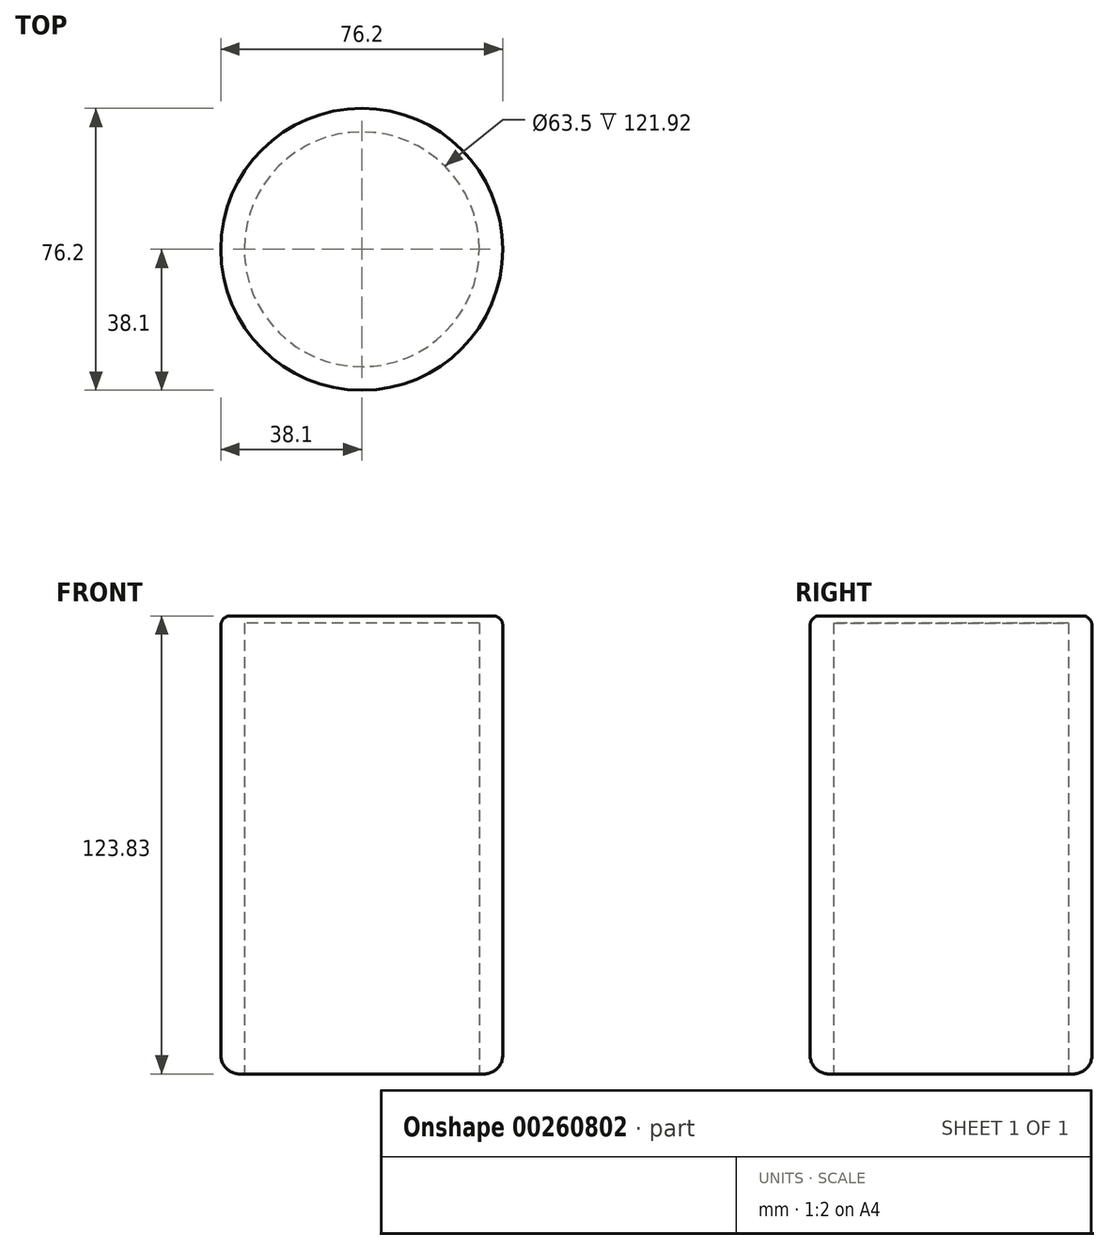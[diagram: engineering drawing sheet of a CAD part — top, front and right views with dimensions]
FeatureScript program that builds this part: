
annotation { "Feature Type Name" : "Feature", "Feature Type Description" : "" }
export const myFeature = defineFeature(function(context is Context, id is Id, definition is map)
    precondition{}
    {
        {
            var Q0;
            Q0=qCreatedBy(makeId("Top.planeOp"),FACE);
            var sketch = newSketch(context, id + "F0", { "sketchPlane" : qUnion([Q0])});
            skCircle(sketch, "E0", {"center": v(0, 0) * mm, "radius": 38.1 * mm});
            skSolve(sketch);
        }
        {
            var Q0;
            Q0=qCreatedBy(makeId("Top.planeOp"),FACE);
            var sketch = newSketch(context, id + "F1", { "sketchPlane" : qUnion([Q0])});
            skCircle(sketch, "E1", {"center": v(0, 0) * mm, "radius": 31.75 * mm});
            skSolve(sketch);
        }
        {
            var Q0;
            Q0 = qSketchRegion(id + "F0", true);
            extrude(context, id + "F2", {"entities" : qUnion([Q0]), "depth" : 123.82 * mm});
        }
        {
            var Q0;
            Q0 = qSketchRegion(id + "F1", true);
            extrude(context, id + "F3", {"entities" : qUnion([Q0]), "operationType" : NewBodyOperationType.REMOVE, "depth" : 121.92 * mm});
        }
        {
            var Q0;
            Q0=makeQuery(id+"F2.opExtrude","CAP_EDGE",EDGE,{"disambiguationData":[OSD([sQuery(id+"F0.wireOp",EDGE,"E0")])],"isStart":true});
            fillet(context, id + "F4", {"entities" : qUnion([Q0]), "radius" : 5.08 * mm, "tangentPropagation" : true, "allowEdgeOverflow" : false});
        }
        {
            var Q0;
            Q0=makeQuery(id+"F2.opExtrude","CAP_EDGE",EDGE,{"disambiguationData":[OSD([sQuery(id+"F0.wireOp",EDGE,"E0")])],"isStart":false});
            fillet(context, id + "F5", {"entities" : qUnion([Q0]), "radius" : 2.54 * mm, "tangentPropagation" : true, "allowEdgeOverflow" : false});
        }
    });
